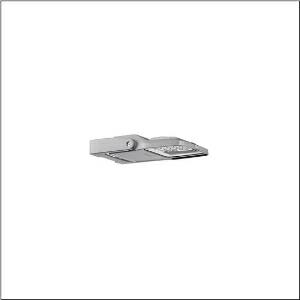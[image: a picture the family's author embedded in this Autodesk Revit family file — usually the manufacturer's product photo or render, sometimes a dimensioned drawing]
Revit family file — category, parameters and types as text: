
# Revit family: floodlight_fl_21_iq_micro___pl64_5xa7762a4e2a_da81
name_source: partatom
category: Lighting Fixtures
units: mm (PartAtom-declared; Revit-internal decimal feet)

## family parameters
Cut with Voids When Loaded = No
Host = Face
Light Source = No
Part Type = Normal
Room Calculation Point = No
Round Connector Dimension = Use Diameter
Shared = No

## types (1)
- --- (1 x LED, 2980 lm, 23.1 W, 4000K)
    Apparent Load = 23 VA
    CIE Flux Codes = 28 80 98 100 100
    Color Rendering = 70
    Color Temperature = 4000K
    Default Elevation = 1800 mm
    Description = Floodlight FL 21 iQ micro, floodlight, primary light control with lens, of PMMA, primary optical cover: protective disc, of toughened safety glass, transparent, light distribution: PL64, light emission: direct distribution, installation type: surface-mounted, LED, High Power LED, rated luminous flux: 2.980lm, luminous efficacy: 129lm/W, light colour: 740, colour temperature: 4000K, control gear: iQ Street-Remote/DALI, control: Auto-Match, Temp-Guard, Night-Set, Smart-Wire, Desk-Remote (wireless, voltage-free reading and setting of iQ features in the workshop via application-optimized NFC function/RFID function), optimised constant luminous flux control (CLO 2.0), Street-Remote, with terminal, 6-pole, mains connection: 220..240V, AC, 50/60Hz, start of lifetime: 23W, end of service life: 24W, reduction: 11W, luminaire housing, of diecast aluminium, powder-coated, Siteco® metallic grey (DB 702S), corrosivity category C5 mid according to DIN EN ISO 12944, suitable for swimming pools, chlorine-resistant, sealing non-destructively replaceable, design bracket, of diecast aluminium, powder-coated, Siteco® metallic grey (DB 702S), protection rating (complete): IP66, insulation class (complete): insulation class II (safety insulation), certification: CE, ENEC, VDE, protection symbol: D, impact resistance: IK07, permissible operating ambient temperature: -40..+40°C, permissible operating ambient temperature for outdoor applications: -40..+50°C, standard: DIN EN 12944, LABS conformity tested according to VDMA 24364:2018-05, packaging unit: 1 piece

Light Distribution: PL64
    Height = 65 mm
    Lamp = 1 x LED
    Lamp Light Flux = 2980 lm
    Lamp Power = 23.1 W
    Lamp count = 1
    Length = 312 mm
    Luminous efficacy = 129 lm/W
    Manufacturer = Siteco
    ModVariant = No
    Model = 5XA7762A4E2A
    Mounting Place = Wall
    Mounting Type = Surface mounted
    Number of Poles = 1
    OnlyDefault = Yes
    Power Factor = 1
    Product Name = Floodlight FL 21 iQ micro | PL64
    Product group = floodlight | wall mounted
    ProductGroupID = 2001
    Protection Class = Protection class II
    Protection Degree = IP 66
    RLX_Detail_Level = 1
    RLX_Emergency_Light_Flux = 0 lm
    RLX_Emergency_Type = 0
    RLX_Emergency_Type_DB = No
    RlxData = <blob elided: 97481 chars, md5=12fd2008>
    Socket = socket
    Standby Power = 0 W
    System Light Flux = 2980 lm
    System Power = 23 W
    Type Comments = factory setting: luminous flux: 100 % | dim-lin: 254 | 455 mA
    Type Image = l_1006878.jpg
    URL = http://relux.com
    VarID = @adj_180506
    Voltage = 0 V
    Weight = 0.00 kg
    Width = 230 mm

## geometry (parser evidence)
native form markers: Blend x4, Sweep x12
no freeform markers — native parametric forms only
